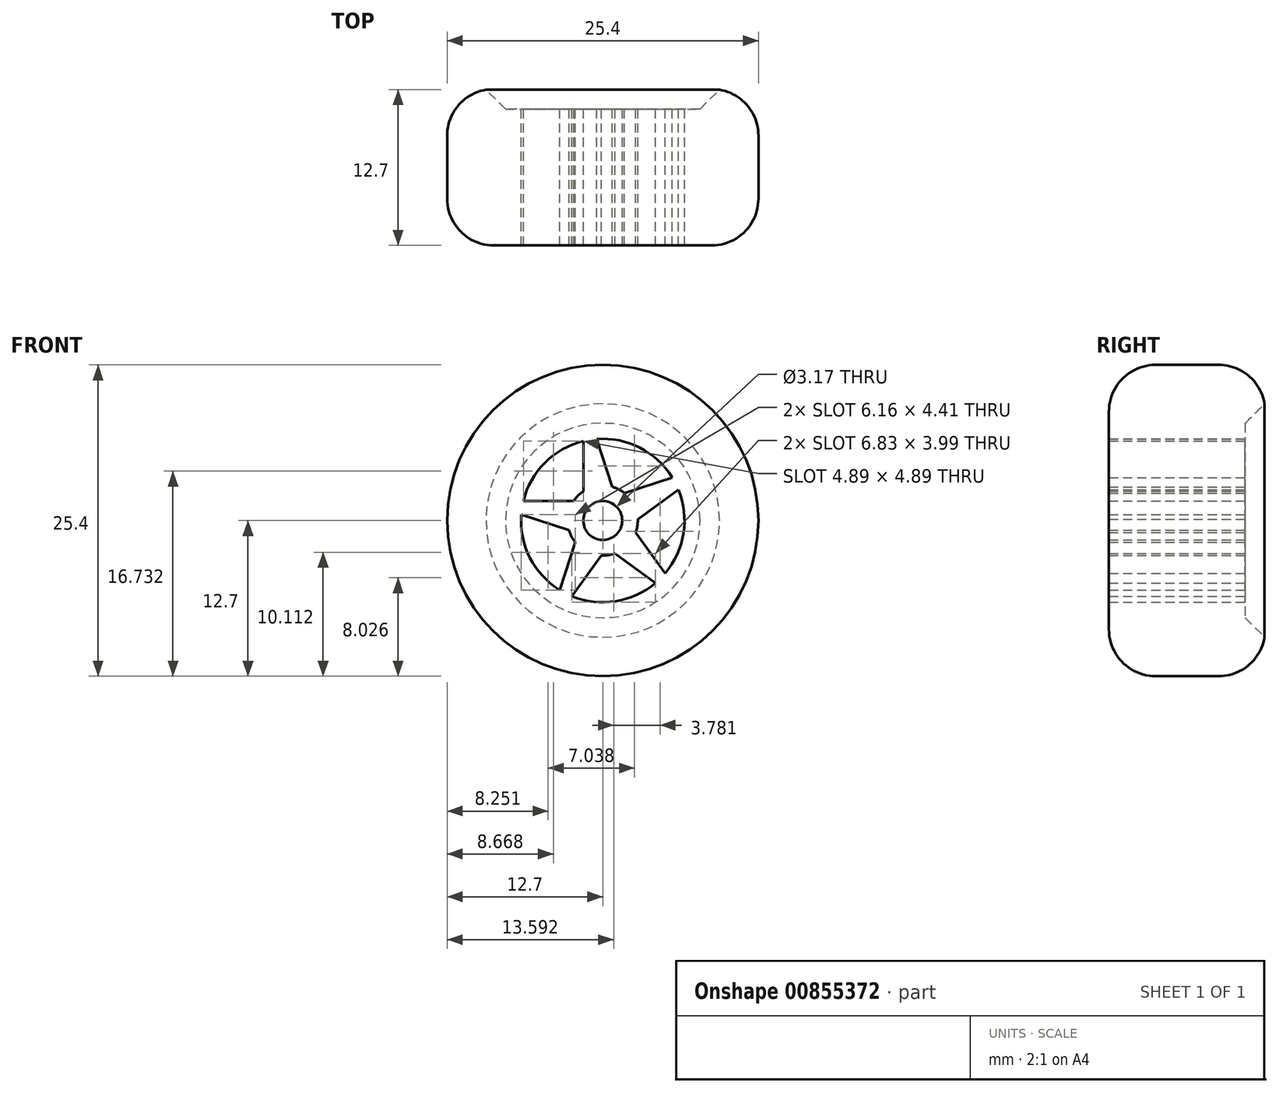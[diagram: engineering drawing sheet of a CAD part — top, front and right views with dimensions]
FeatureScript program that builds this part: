
annotation { "Feature Type Name" : "Feature", "Feature Type Description" : "" }
export const myFeature = defineFeature(function(context is Context, id is Id, definition is map)
    precondition{}
    {
        {
            var Q0;
            Q0=qCreatedBy(makeId("Right.planeOp"),FACE);
            var sketch = newSketch(context, id + "F0", { "sketchPlane" : qUnion([Q0])});
            skLineSegment(sketch, "E0", {"start": v(0, 0) * mm, "end": v(0, 12.7) * mm});
            skLineSegment(sketch, "E1", {"start": v(0, 12.7) * mm, "end": v(12.7, 12.7) * mm});
            skLineSegment(sketch, "E2", {"start": v(12.7, 12.7) * mm, "end": v(12.7, 9.53) * mm});
            skLineSegment(sketch, "E3", {"start": v(12.7, 9.53) * mm, "end": v(11.11, 7.94) * mm});
            skLineSegment(sketch, "E4", {"start": v(11.11, 7.94) * mm, "end": v(11.11, 0) * mm});
            skLineSegment(sketch, "E5", {"start": v(11.11, 0) * mm, "end": v(0, 0) * mm});
            skSolve(sketch);
        }
        {
            var Q0;
            Q0=makeQuery(id+"F0.imprint","IMPRINT",FACE,{"disambiguationData":[TD([[makeQuery(id+"F0.imprint","IMPRINT",EDGE,{"derivedFrom":sQuery(id+"F0.wireOp",EDGE,"E0")}),-1.0]])]});
            var Q1;
            Q1=sQuery(id+"F0.wireOp",EDGE,"E5");
            revolve(context, id + "F1", {"surfaceOperationType" : NewSurfaceOperationType.NEW, "entities" : qUnion([Q0]), "axis" : qUnion([Q1]), "revolveType" : RevolveType.FULL});
        }
        {
            var Q0;
            Q0=makeQuery(id+"F1.opRevolve","SWEPT_EDGE",EDGE,{"disambiguationData":[OSD([sQuery(id+"F0.wireOp",EDGE,"E0"),sQuery(id+"F0.wireOp",EDGE,"E1")])]});
            var Q1;
            Q1=makeQuery(id+"F1.opRevolve","SWEPT_EDGE",EDGE,{"disambiguationData":[OSD([sQuery(id+"F0.wireOp",EDGE,"E1"),sQuery(id+"F0.wireOp",EDGE,"E2")])]});
            fillet(context, id + "F2", {"entities" : qUnion([Q0, Q1]), "radius" : 3.8 * mm, "tangentPropagation" : true, "allowEdgeOverflow" : false});
        }
        {
            var Q0;
            Q0=makeQuery(id+"F1.opRevolve","SWEPT_FACE",FACE,{"disambiguationData":[OSD([sQuery(id+"F0.wireOp",EDGE,"E4")])]});
            var sketch = newSketch(context, id + "F3", { "sketchPlane" : qUnion([Q0])});
            skCircle(sketch, "E6", {"center": v(0, 0) * mm, "radius": 1.59 * mm});
            skSolve(sketch);
        }
        {
            var Q0;
            Q0=makeQuery(id+"F3.imprint","IMPRINT",FACE,{"disambiguationData":[TD([[makeQuery(id+"F3.imprint","IMPRINT",EDGE,{"derivedFrom":sQuery(id+"F3.wireOp",EDGE,"E6")}),1.0]])]});
            extrude(context, id + "F4", {"entities" : qUnion([Q0]), "operationType" : NewBodyOperationType.REMOVE, "oppositeDirection" : true, "depth" : 12.7 * mm, "offsetDistance" : 25.4 * mm});
        }
        {
            var Q0;
            Q0=makeQuery(id+"F1.opRevolve","SWEPT_FACE",FACE,{"disambiguationData":[OSD([sQuery(id+"F0.wireOp",EDGE,"E4")])]});
            var sketch = newSketch(context, id + "F5", { "sketchPlane" : qUnion([Q0])});
            skLineSegment(sketch, "E7", {"start": v(2.38, 1.59) * mm, "end": v(6.48, 1.59) * mm});
            skLineSegment(sketch, "E8", {"start": v(1.59, 2.38) * mm, "end": v(1.59, 6.48) * mm});
            skPoint(sketch, "E9.start.orphan", {"position": v(0, -1.59) * mm});
            skArc(sketch, "E10", {"start": v(6.48, 1.59) * mm, "mid": v(4.71, 4.71) * mm, "end": v(1.59, 6.48) * mm});
            skPoint(sketch, "E11.orphan", {"position": v(0, 1.59) * mm});
            skPoint(sketch, "E12.orphan", {"position": v(1.59, 0) * mm});
            skArc(sketch, "E13", {"start": v(2.38, 1.59) * mm, "mid": v(2.02, 2.02) * mm, "end": v(1.59, 2.38) * mm});
            skLineSegment(sketch, "E14.1.0", {"start": v(-1.77, 2.24) * mm, "end": v(-5.67, 3.51) * mm});
            skArc(sketch, "E14.1.1", {"start": v(-0.78, 2.75) * mm, "mid": v(-1.3, 2.55) * mm, "end": v(-1.77, 2.24) * mm});
            skLineSegment(sketch, "E14.1.2", {"start": v(-0.78, 2.75) * mm, "end": v(0.5, 6.65) * mm});
            skArc(sketch, "E14.1.3", {"start": v(0.5, 6.65) * mm, "mid": v(-3.03, 5.94) * mm, "end": v(-5.67, 3.51) * mm});
            skLineSegment(sketch, "E14.2.0", {"start": v(-2.68, -0.99) * mm, "end": v(-5.1, -4.3) * mm});
            skArc(sketch, "E14.2.1", {"start": v(-2.86, 0.11) * mm, "mid": v(-2.82, -0.45) * mm, "end": v(-2.68, -0.99) * mm});
            skLineSegment(sketch, "E14.2.2", {"start": v(-2.86, 0.11) * mm, "end": v(-6.17, 2.52) * mm});
            skArc(sketch, "E14.2.3", {"start": v(-6.17, 2.52) * mm, "mid": v(-6.59, -1.04) * mm, "end": v(-5.1, -4.3) * mm});
            skLineSegment(sketch, "E14.3.0", {"start": v(0.11, -2.86) * mm, "end": v(2.52, -6.17) * mm});
            skArc(sketch, "E14.3.1", {"start": v(-0.99, -2.68) * mm, "mid": v(-0.45, -2.82) * mm, "end": v(0.11, -2.86) * mm});
            skLineSegment(sketch, "E14.3.2", {"start": v(-0.99, -2.68) * mm, "end": v(-4.3, -5.1) * mm});
            skArc(sketch, "E14.3.3", {"start": v(-4.3, -5.1) * mm, "mid": v(-1.04, -6.59) * mm, "end": v(2.52, -6.17) * mm});
            skLineSegment(sketch, "E15.1.4.0", {"start": v(2.75, -0.78) * mm, "end": v(6.65, 0.5) * mm});
            skArc(sketch, "E15.3.4.0", {"start": v(2.24, -1.77) * mm, "mid": v(2.55, -1.3) * mm, "end": v(2.75, -0.78) * mm});
            skLineSegment(sketch, "E15.7.4.0", {"start": v(2.24, -1.77) * mm, "end": v(3.51, -5.67) * mm});
            skArc(sketch, "E15.10.4.0", {"start": v(3.51, -5.67) * mm, "mid": v(5.94, -3.03) * mm, "end": v(6.65, 0.5) * mm});
            skSolve(sketch);
        }
        {
            var Q0;
            Q0=makeQuery(id+"F5.imprint","IMPRINT",FACE,{"disambiguationData":[TD([[makeQuery(id+"F5.imprint","IMPRINT",EDGE,{"derivedFrom":sQuery(id+"F5.wireOp",EDGE,"E14.1.0")}),-1.0]])]});
            var Q1;
            Q1=makeQuery(id+"F5.imprint","IMPRINT",FACE,{"disambiguationData":[TD([[makeQuery(id+"F5.imprint","IMPRINT",EDGE,{"derivedFrom":sQuery(id+"F5.wireOp",EDGE,"E7")}),1.0]])]});
            var Q2;
            Q2=makeQuery(id+"F5.imprint","IMPRINT",FACE,{"disambiguationData":[TD([[makeQuery(id+"F5.imprint","IMPRINT",EDGE,{"derivedFrom":sQuery(id+"F5.wireOp",EDGE,"E14.2.0")}),-1.0]])]});
            var Q3;
            Q3=makeQuery(id+"F5.imprint","IMPRINT",FACE,{"disambiguationData":[TD([[makeQuery(id+"F5.imprint","IMPRINT",EDGE,{"derivedFrom":sQuery(id+"F5.wireOp",EDGE,"E14.3.0")}),-1.0]])]});
            var Q4;
            Q4=makeQuery(id+"F5.imprint","IMPRINT",FACE,{"disambiguationData":[TD([[makeQuery(id+"F5.imprint","IMPRINT",EDGE,{"derivedFrom":sQuery(id+"F5.wireOp",EDGE,"E15.1.4.0")}),-1.0]])]});
            extrude(context, id + "F6", {"entities" : qUnion([Q0, Q1, Q2, Q3, Q4]), "operationType" : NewBodyOperationType.REMOVE, "oppositeDirection" : true, "depth" : 25.4 * mm, "offsetDistance" : 25.4 * mm});
        }
    });
